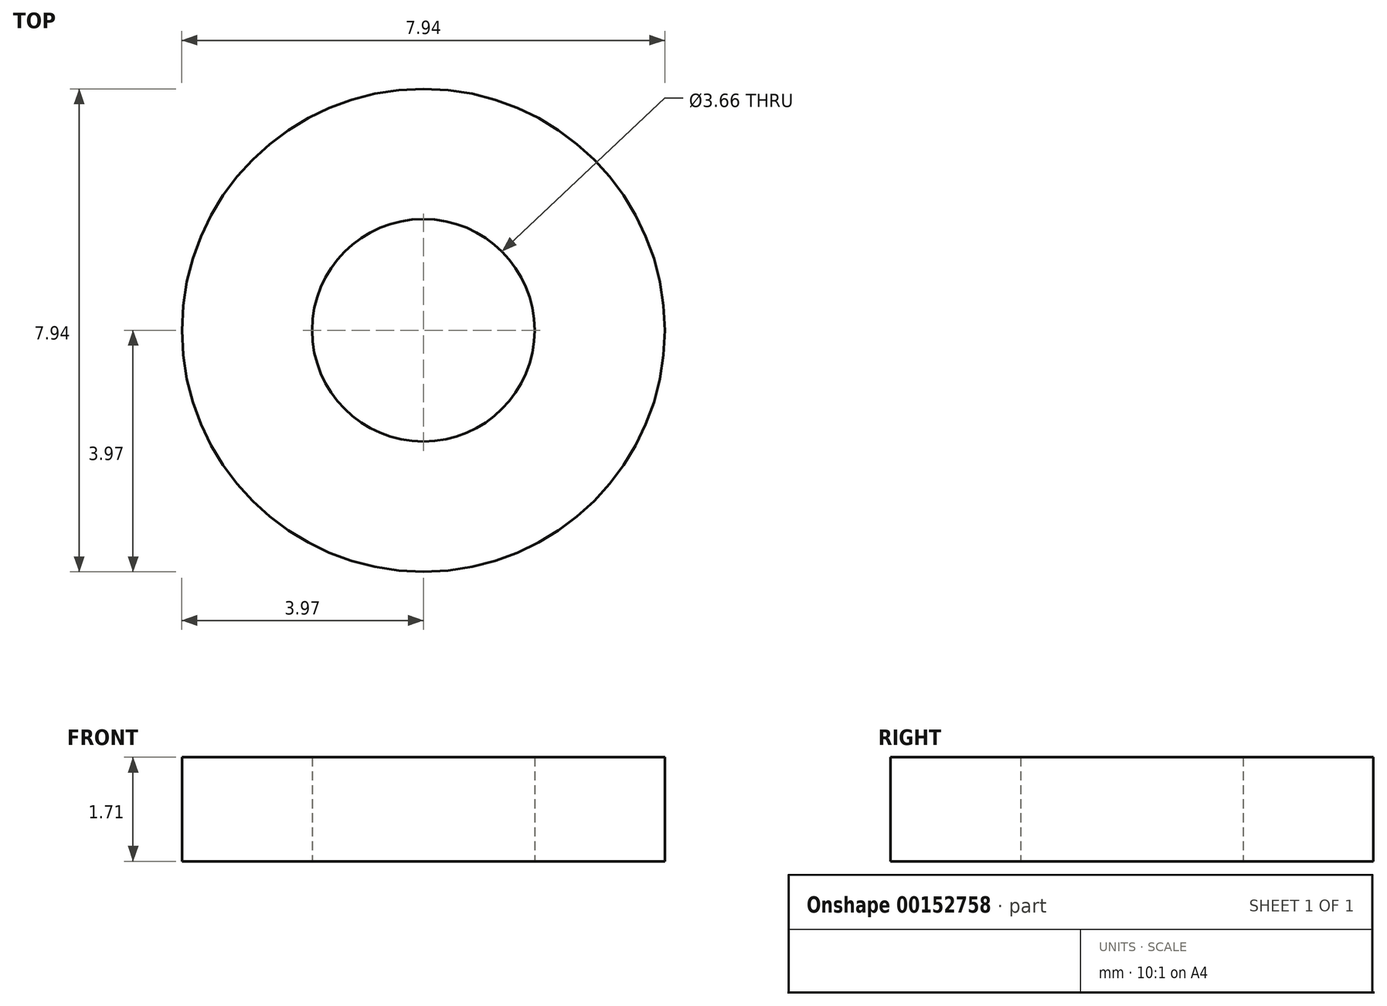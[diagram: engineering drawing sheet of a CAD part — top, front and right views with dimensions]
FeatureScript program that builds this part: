
annotation { "Feature Type Name" : "Feature", "Feature Type Description" : "" }
export const myFeature = defineFeature(function(context is Context, id is Id, definition is map)
    precondition{}
    {
        {
            var Q0;
            Q0=qCreatedBy(makeId("Top.planeOp"),FACE);
            var sketch = newSketch(context, id + "F0", { "sketchPlane" : qUnion([Q0])});
            skCircle(sketch, "E0", {"center": v(0, 0) * mm, "radius": 1.83 * mm});
            skCircle(sketch, "E1", {"center": v(0, 0) * mm, "radius": 3.97 * mm});
            skSolve(sketch);
        }
        {
            var Q0;
            Q0=qSketchRegion(id+"F0",true);
            extrude(context, id + "F1", {"entities" : qUnion([Q0]), "depth" : 1.7 * mm});
        }
    });
